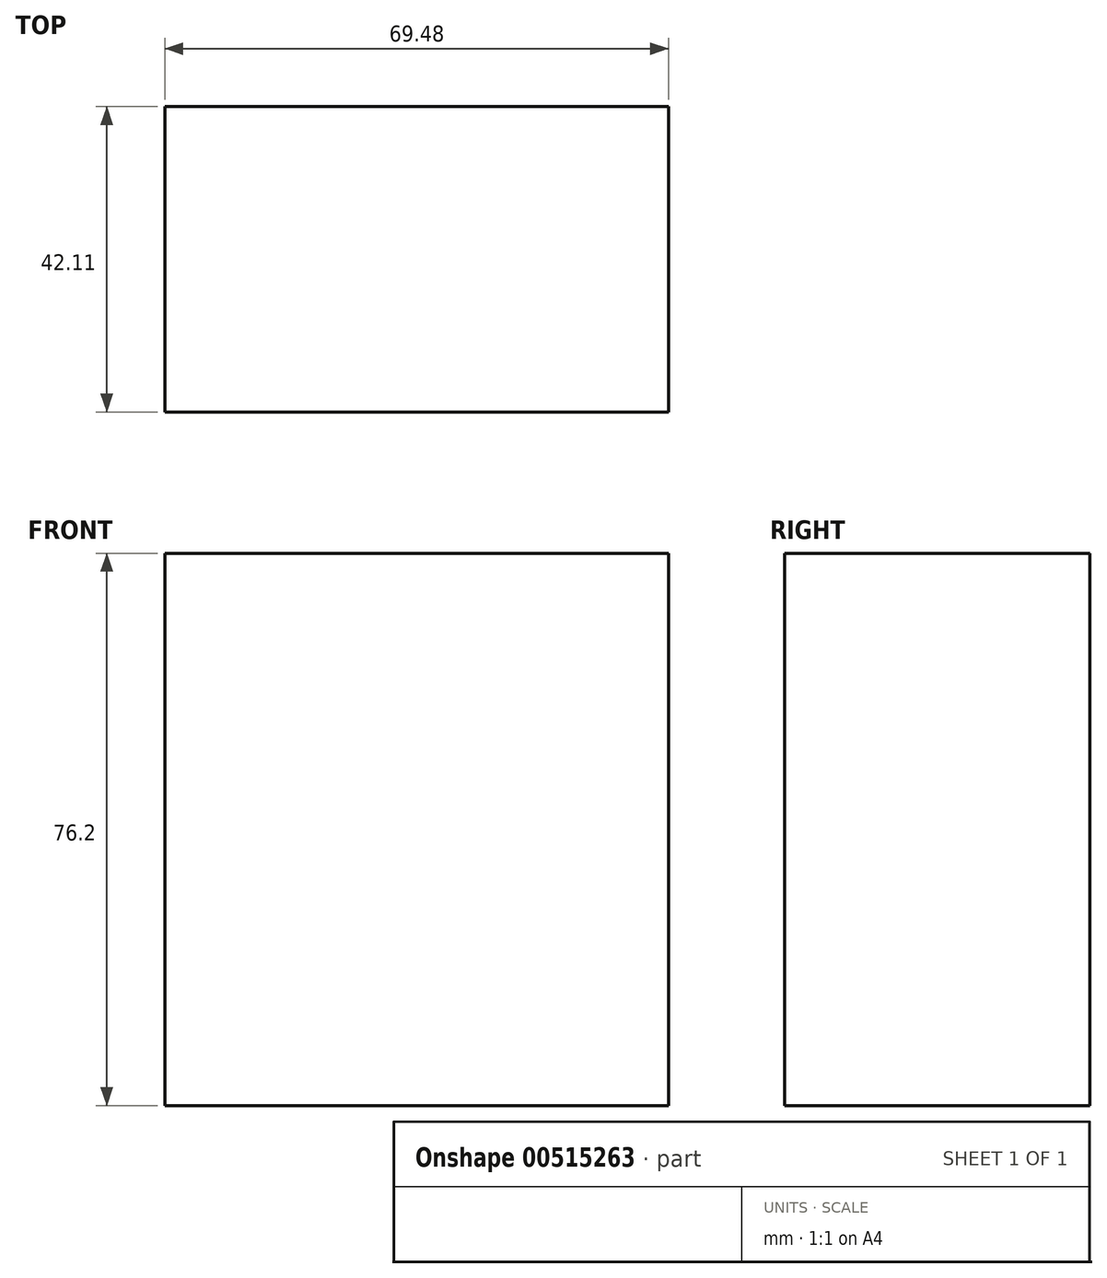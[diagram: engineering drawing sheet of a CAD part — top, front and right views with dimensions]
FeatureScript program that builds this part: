
annotation { "Feature Type Name" : "Feature", "Feature Type Description" : "" }
export const myFeature = defineFeature(function(context is Context, id is Id, definition is map)
    precondition{}
    {
        {
            var Q0;
            Q0=qCreatedBy(makeId("Top.planeOp"),FACE);
            var sketch = newSketch(context, id + "F0", { "sketchPlane" : qUnion([Q0])});
            skLineSegment(sketch, "E0.bottom", {"start": v(-34.6, -20.75) * mm, "end": v(34.9, -20.75) * mm});
            skLineSegment(sketch, "E0.top", {"start": v(-34.6, 21.36) * mm, "end": v(34.9, 21.36) * mm});
            skLineSegment(sketch, "E0.left", {"start": v(-34.6, -20.75) * mm, "end": v(-34.6, 21.36) * mm});
            skLineSegment(sketch, "E0.right", {"start": v(34.9, -20.75) * mm, "end": v(34.9, 21.36) * mm});
            skSolve(sketch);
        }
        {
            var Q0;
            Q0=makeQuery(id+"F0.imprint","IMPRINT",FACE,{"disambiguationData":[TD([[makeQuery(id+"F0.imprint","IMPRINT",EDGE,{"derivedFrom":sQuery(id+"F0.wireOp",EDGE,"E0.bottom")}),1.0]])]});
            extrude(context, id + "F1", {"entities" : qUnion([Q0]), "depth" : 76.2 * mm, "offsetDistance" : 25.4 * mm});
        }
    });
